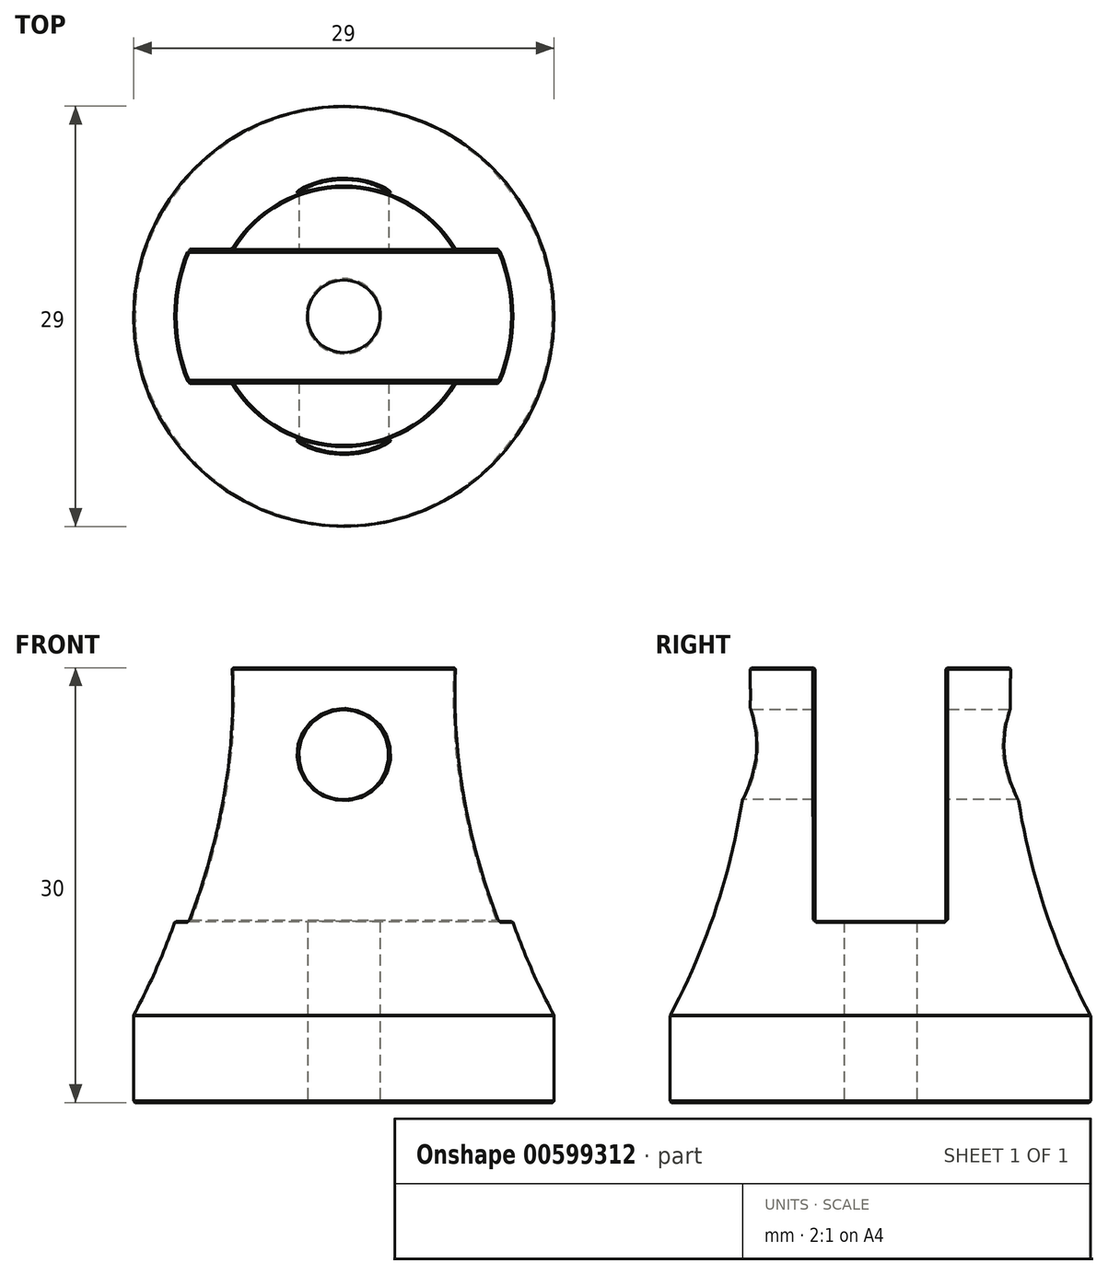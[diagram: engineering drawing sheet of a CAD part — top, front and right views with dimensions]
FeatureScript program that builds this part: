
annotation { "Feature Type Name" : "Feature", "Feature Type Description" : "" }
export const myFeature = defineFeature(function(context is Context, id is Id, definition is map)
    precondition{}
    {
        {
            var Q0;
            Q0=qCreatedBy(makeId("Front.planeOp"),FACE);
            var sketch = newSketch(context, id + "F0", { "sketchPlane" : qUnion([Q0])});
            skLineSegment(sketch, "E0", {"start": v(0, 0) * mm, "end": v(0, 30) * mm, "construction": true});
            skLineSegment(sketch, "E1", {"start": v(-14.5, 0) * mm, "end": v(-2.5, 0) * mm});
            skLineSegment(sketch, "E2", {"start": v(-2.5, 0) * mm, "end": v(-2.5, 15) * mm});
            skLineSegment(sketch, "E3", {"start": v(-2.5, 15) * mm, "end": v(0, 15) * mm});
            skLineSegment(sketch, "E4", {"start": v(0, 15) * mm, "end": v(0, 30) * mm});
            skLineSegment(sketch, "E5", {"start": v(-14.5, 0) * mm, "end": v(-14.5, 6) * mm});
            skLineSegment(sketch, "E6", {"start": v(0, 30) * mm, "end": v(-9, 30) * mm});
            skArc(sketch, "E7", {"start": v(-14.5, 6) * mm, "mid": v(-10.15, 17.63) * mm, "end": v(-9, 30) * mm});
            skSolve(sketch);
        }
        {
            var Q0;
            Q0=makeQuery(id+"F0.imprint","IMPRINT",FACE,{"disambiguationData":[TD([[makeQuery(id+"F0.imprint","IMPRINT",EDGE,{"derivedFrom":sQuery(id+"F0.wireOp",EDGE,"E1")}),1.0]])]});
            var Q1;
            Q1=sQuery(id+"F0.wireOp",EDGE,"E0");
            revolve(context, id + "F1", {"entities" : qUnion([Q0]), "axis" : qUnion([Q1]), "revolveType" : RevolveType.FULL});
        }
        {
            var Q0;
            Q0=qCreatedBy(makeId("Right.planeOp"),FACE);
            var sketch = newSketch(context, id + "F2", { "sketchPlane" : qUnion([Q0])});
            skLineSegment(sketch, "E8", {"start": v(0, 0) * mm, "end": v(0, 30) * mm, "construction": true});
            skLineSegment(sketch, "E9.bottom", {"start": v(0, 30) * mm, "end": v(-4.5, 30) * mm});
            skLineSegment(sketch, "E9.top", {"start": v(0, 12.5) * mm, "end": v(-4.5, 12.5) * mm});
            skLineSegment(sketch, "E9.left", {"start": v(0, 30) * mm, "end": v(0, 12.5) * mm});
            skLineSegment(sketch, "E9.right", {"start": v(-4.5, 30) * mm, "end": v(-4.5, 12.5) * mm});
            skLineSegment(sketch, "E10.MirrorCS", {"start": v(4.5, 30) * mm, "end": v(4.5, 12.5) * mm});
            skLineSegment(sketch, "E11.MirrorCS", {"start": v(0, 30) * mm, "end": v(4.5, 30) * mm});
            skLineSegment(sketch, "E12.MirrorCS", {"start": v(0, 12.5) * mm, "end": v(4.5, 12.5) * mm});
            skSolve(sketch);
        }
        {
            var Q0;
            Q0 = qSketchRegion(id + "F2", true);
            extrude(context, id + "F3", {"entities" : qUnion([Q0]), "operationType" : NewBodyOperationType.REMOVE, "endBound" : BoundingType.SYMMETRIC, "oppositeDirection" : true, "depth" : 35 * mm, "offsetDistance" : 25 * mm});
        }
        {
            var Q0;
            Q0=qCreatedBy(makeId("Front.planeOp"),FACE);
            var sketch = newSketch(context, id + "F4", { "sketchPlane" : qUnion([Q0])});
            skLineSegment(sketch, "E13", {"start": v(0, 0) * mm, "end": v(0, 30) * mm, "construction": true});
            skCircle(sketch, "E14", {"center": v(0, 24) * mm, "radius": 3.1 * mm});
            skSolve(sketch);
        }
        {
            var Q0;
            Q0=makeQuery(id+"F4.imprint","IMPRINT",FACE,{"disambiguationData":[TD([[makeQuery(id+"F4.imprint","IMPRINT",EDGE,{"derivedFrom":sQuery(id+"F4.wireOp",EDGE,"E14")}),1.0]])]});
            extrude(context, id + "F5", {"entities" : qUnion([Q0]), "operationType" : NewBodyOperationType.REMOVE, "endBound" : BoundingType.SYMMETRIC, "oppositeDirection" : true, "depth" : 25 * mm, "offsetDistance" : 25 * mm});
        }
        {
            var Q0;
            Q0=makeQuery(id+"F1.opRevolve","SWEPT_FACE",FACE,{"disambiguationData":[OSD([sQuery(id+"F0.wireOp",EDGE,"E7")])]});
            var Q1;
            Q1=makeQuery(id+"F3.boolean.opBoolean","COPY",FACE,{"derivedFrom":makeQuery(id+"F3.opExtrude","SWEPT_FACE",FACE,{"disambiguationData":[OSD([sQuery(id+"F2.wireOp",EDGE,"E9.right")])]})});
            var Q2;
            Q2=makeQuery(id+"F3.boolean.opBoolean","COPY",FACE,{"derivedFrom":makeQuery(id+"F3.opExtrude","SWEPT_FACE",FACE,{"disambiguationData":[OSD([sQuery(id+"F2.wireOp",EDGE,"E10.MirrorCS")])]})});
            var Q3;
            Q3=makeQuery(id+"F1.opRevolve","SWEPT_FACE",FACE,{"disambiguationData":[OSD([sQuery(id+"F0.wireOp",EDGE,"E5")])]});
            var Q4;
            Q4=makeQuery(id+"F1.opRevolve","SWEPT_FACE",FACE,{"disambiguationData":[OSD([sQuery(id+"F0.wireOp",EDGE,"E1")])]});
            chamfer(context, id + "F6", {"entities" : qUnion([Q0, Q1, Q2, Q3, Q4]), "width" : .1 * mm, "tangentPropagation" : true});
        }
    });
